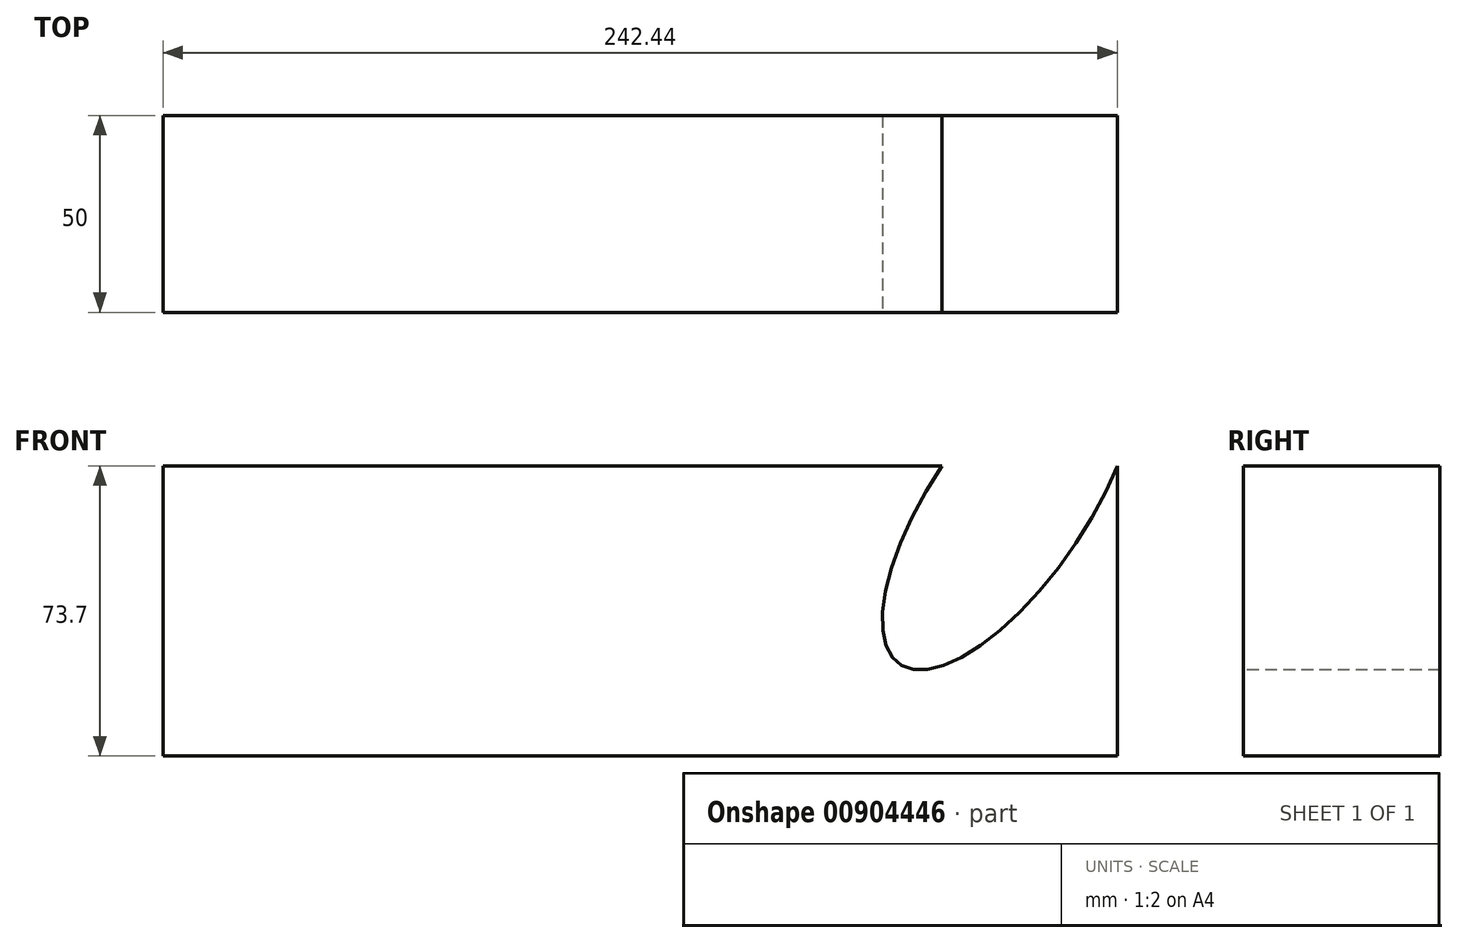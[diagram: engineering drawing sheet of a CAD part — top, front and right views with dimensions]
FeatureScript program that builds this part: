
annotation { "Feature Type Name" : "Feature", "Feature Type Description" : "" }
export const myFeature = defineFeature(function(context is Context, id is Id, definition is map)
    precondition{}
    {
        {
            var Q0;
            Q0=qCreatedBy(makeId("Front.planeOp"),FACE);
            var sketch = newSketch(context, id + "F0", { "sketchPlane" : qUnion([Q0])});
            skLineSegment(sketch, "E0.bottom", {"start": v(121.22, 36.85) * mm, "end": v(-121.22, 36.85) * mm});
            skLineSegment(sketch, "E0.top", {"start": v(121.22, -36.85) * mm, "end": v(-121.22, -36.85) * mm});
            skLineSegment(sketch, "E0.left", {"start": v(121.22, 36.85) * mm, "end": v(121.22, -36.85) * mm});
            skLineSegment(sketch, "E0.right", {"start": v(-121.22, 36.85) * mm, "end": v(-121.22, -36.85) * mm});
            skPoint(sketch, "E0.middle", {"position": v(0, 0) * mm});
            skEllipticalArc(sketch, "E1", {});
            const initialGuessF0  = {"E1": [0.09365588426589966, 0.027004241943359375, 0.8246462398902478, -0.5656488124577616, 0.019601607878605275, 0.049101100044187065, 3.172245059419879, 0.5039022973145002]};
            skSetInitialGuess(sketch, initialGuessF0);
            skSolve(sketch);
        }
        {
            var Q0;
            Q0=makeQuery(id+"F0.imprint","IMPRINT",FACE,{"disambiguationData":[TD([[makeQuery(id+"F0.imprint","IMPRINT",EDGE,{"derivedFrom":sQuery(id+"F0.wireOp",EDGE,"E0.top")}),-1.0]])]});
            extrude(context, id + "F1", {"entities" : qUnion([Q0]), "depth" : 50 * mm, "offsetDistance" : 25.4 * mm});
        }
    });
